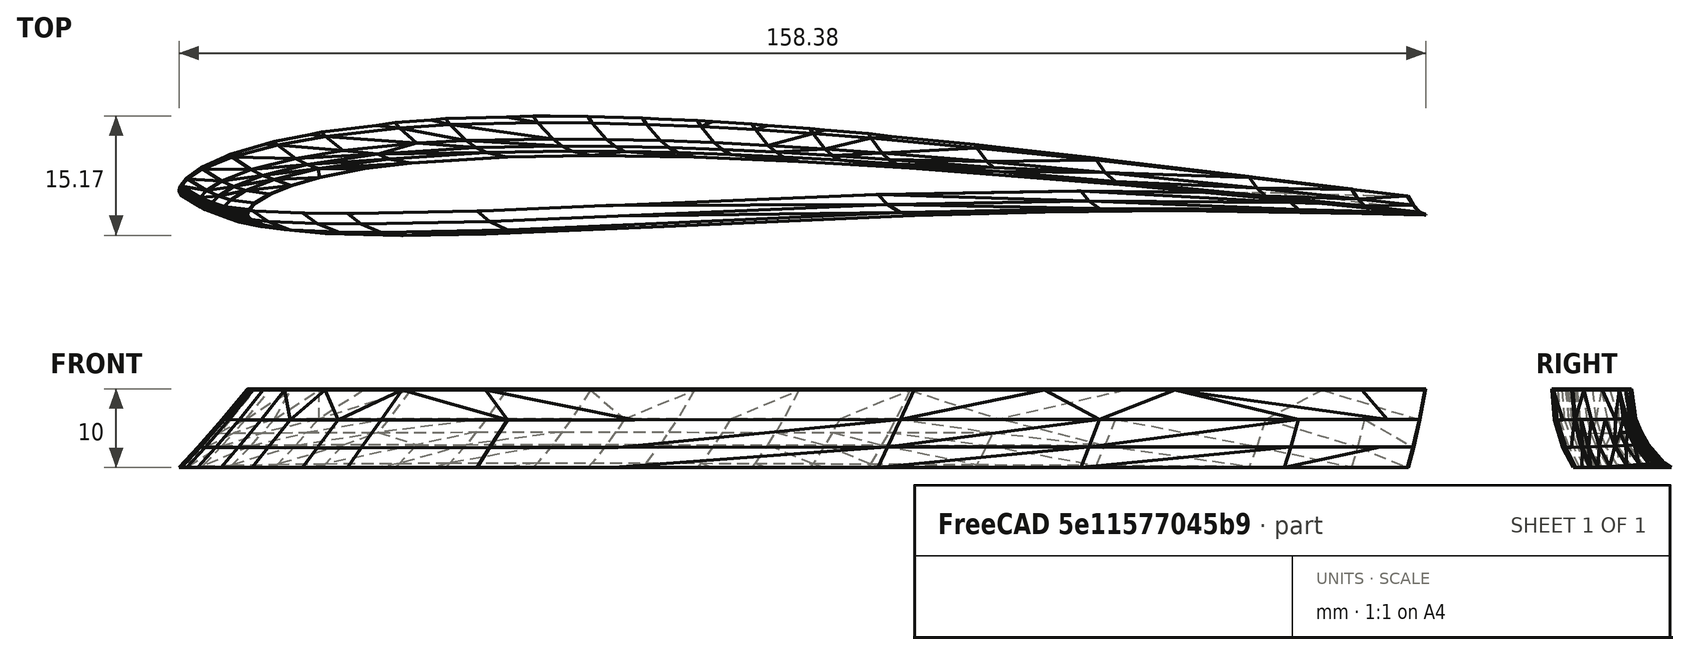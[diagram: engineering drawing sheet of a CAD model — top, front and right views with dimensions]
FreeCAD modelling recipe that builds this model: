
FCSTD DOCUMENT  (FreeCAD 0.19R24276 (Git))
Label: Con_left_winglet_default
License: All rights reserved
LicenseURL: http://en.wikipedia.org/wiki/All_rights_reserved
objects: Mesh::Feature×1, Sketcher::SketchObject×1, Part::Extrusion×1, Part::Feature×1, Part::Cut×1
note: 4 computed .brp shape members not serialized (recipe doc carries the construction recipe); baked Part::Feature solids carry a one-line shape summary decoded from their .brp

FEATURE [Mesh::Feature] Con_left_winglet_default
FEATURE [Sketcher::SketchObject] Sketch
  FullyConstrained = true
  MapMode = 5
  Placement = pos=(0,0,0) rot=(1,0,0;1.5708rad)
  sketch-geometry (8):
    g0: LineSegment StartX=100 StartY=260 StartZ=0 EndX=425 EndY=260 EndZ=0
    g1: LineSegment StartX=425 StartY=260 StartZ=0 EndX=425 EndY=60 EndZ=0
    g2: LineSegment StartX=425 StartY=60 StartZ=0 EndX=100 EndY=60 EndZ=0
    g3: LineSegment StartX=100 StartY=60 StartZ=0 EndX=100 EndY=260 EndZ=0
    g4: LineSegment StartX=100 StartY=50 StartZ=0 EndX=425 EndY=50 EndZ=0
    g5: LineSegment StartX=425 StartY=50 StartZ=0 EndX=425 EndY=0 EndZ=0
    g6: LineSegment StartX=425 StartY=0 StartZ=0 EndX=100 EndY=0 EndZ=0
    g7: LineSegment StartX=100 StartY=0 StartZ=0 EndX=100 EndY=50 EndZ=0
  constraints (24):
    c: Coincident(g0,g1)
    c: Coincident(g1,g2)
    c: Coincident(g2,g3)
    c: Coincident(g3,g0)
    c: Horizontal(g0)
    c: Horizontal(g2)
    c: Vertical(g1)
    c: Vertical(g3)
    c: DistanceX(g-1,g2) = 100
    c: DistanceX(g2,g2) = 325
    c: DistanceY(g3,g3) = 200
    c: DistanceY(g-1,g2) = 60
    c: Coincident(g4,g5)
    c: Coincident(g5,g6)
    c: Coincident(g6,g7)
    c: Coincident(g7,g4)
    c: Horizontal(g4)
    c: Horizontal(g6)
    c: Vertical(g5)
    c: Vertical(g7)
    c: PointOnObject(g6,g-1)
    c: DistanceX(g-1,g4) = 100
    c: DistanceX(g6,g6) = 325
    c: DistanceY(g5,g5) = 50
FEATURE [Part::Extrusion] Extrude
  Base = -> Sketch
  Dir = (0,-1,2e-16)
  DirMode = 2
  FaceMakerClass = Part::FaceMakerBullseye
  LengthFwd = 1100
  LengthRev = 0
  Solid = true
  Symmetric = false
FEATURE [Part::Feature] Con_left_winglet_default001
  shape: bbox 215.9 x 77.66 x 184.7 mm, 1678 faces, 0 solids (baked)
FEATURE [Part::Cut] Cut
  Base = -> Con_left_winglet_default001
  Tool = -> Extrude
